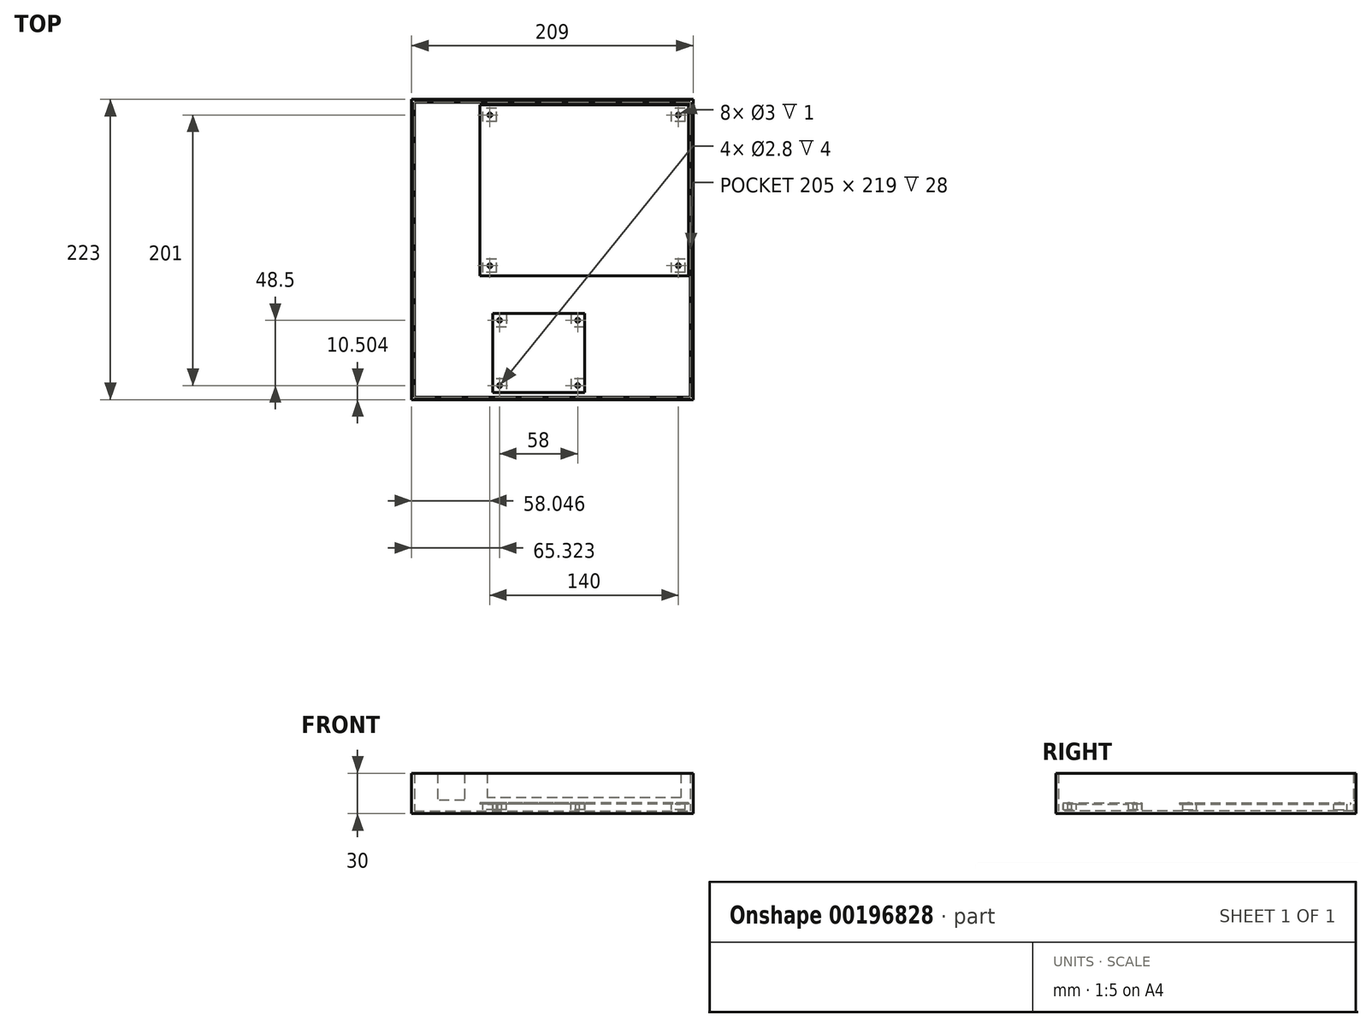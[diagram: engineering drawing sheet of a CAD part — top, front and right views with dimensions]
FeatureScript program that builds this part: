
annotation { "Feature Type Name" : "Feature", "Feature Type Description" : "" }
export const myFeature = defineFeature(function(context is Context, id is Id, definition is map)
    precondition{}
    {
        {
            var Q0;
            Q0=qCreatedBy(makeId("Top.planeOp"),FACE);
            var sketch = newSketch(context, id + "F0", { "sketchPlane" : qUnion([Q0])});
            skLineSegment(sketch, "E0.bottom", {"start": v(9.11, -36.76) * mm, "end": v(-58.89, -36.76) * mm});
            skLineSegment(sketch, "E0.top", {"start": v(9.11, 21.74) * mm, "end": v(-58.89, 21.74) * mm});
            skLineSegment(sketch, "E0.left", {"start": v(9.11, -36.76) * mm, "end": v(9.11, 21.74) * mm});
            skLineSegment(sketch, "E0.right", {"start": v(-58.89, -36.76) * mm, "end": v(-58.89, 21.74) * mm});
            skPoint(sketch, "E0.middle", {"position": v(-24.89, -7.5) * mm});
            skLineSegment(sketch, "E1.bottom", {"start": v(86.34, 49.74) * mm, "end": v(-68.66, 49.74) * mm});
            skLineSegment(sketch, "E1.top", {"start": v(86.34, 176.74) * mm, "end": v(-68.66, 176.74) * mm});
            skLineSegment(sketch, "E1.left", {"start": v(86.34, 49.74) * mm, "end": v(86.34, 176.74) * mm});
            skLineSegment(sketch, "E1.right", {"start": v(-68.66, 49.74) * mm, "end": v(-68.66, 176.74) * mm});
            skPoint(sketch, "E1.middle", {"position": v(8.84, 113.24) * mm});
            skLineSegment(sketch, "E2.bottom", {"start": v(-72.66, -35.95) * mm, "end": v(-114.66, -35.95) * mm, "construction": true});
            skLineSegment(sketch, "E2.top", {"start": v(-72.66, 141.05) * mm, "end": v(-114.66, 141.05) * mm, "construction": true});
            skLineSegment(sketch, "E2.left", {"start": v(-72.66, -35.95) * mm, "end": v(-72.66, 141.05) * mm, "construction": true});
            skLineSegment(sketch, "E2.right", {"start": v(-114.66, -35.95) * mm, "end": v(-114.66, 141.05) * mm, "construction": true});
            skPoint(sketch, "E2.middle", {"position": v(-93.66, 52.55) * mm});
            skLineSegment(sketch, "E3.bottom", {"start": v(-74.66, -33.95) * mm, "end": v(-112.66, -33.95) * mm, "construction": true});
            skLineSegment(sketch, "E3.top", {"start": v(-74.66, 139.05) * mm, "end": v(-112.66, 139.05) * mm, "construction": true});
            skLineSegment(sketch, "E3.left", {"start": v(-74.66, -33.95) * mm, "end": v(-74.66, 139.05) * mm, "construction": true});
            skLineSegment(sketch, "E3.right", {"start": v(-112.66, -33.95) * mm, "end": v(-112.66, 139.05) * mm, "construction": true});
            skSolve(sketch);
        }
        {
            var Q0;
            Q0 = qSketchRegion(id + "F0", true);
            extrude(context, id + "F1", {"entities" : qUnion([Q0]), "depth" : 1 * mm});
        }
        {
            var Q0;
            Q0=makeQuery(id+"F1.opExtrude","CAP_FACE",FACE,{"disambiguationData":[OSD([sQuery(id+"F0.wireOp",EDGE,"E0.bottom"),sQuery(id+"F0.wireOp",EDGE,"E0.top"),sQuery(id+"F0.wireOp",EDGE,"E0.left"),sQuery(id+"F0.wireOp",EDGE,"E0.right")])],"isStart":true});
            var sketch = newSketch(context, id + "F2", { "sketchPlane" : qUnion([Q0])});
            skLineSegment(sketch, "E4.bottom", {"start": v(-48.89, 26.76) * mm, "end": v(-58.89, 26.76) * mm});
            skLineSegment(sketch, "E4.top", {"start": v(-48.89, 36.76) * mm, "end": v(-58.89, 36.76) * mm});
            skLineSegment(sketch, "E4.left", {"start": v(-48.89, 26.76) * mm, "end": v(-48.89, 36.76) * mm});
            skLineSegment(sketch, "E4.right", {"start": v(-58.89, 26.76) * mm, "end": v(-58.89, 36.76) * mm});
            skPoint(sketch, "E4.middle", {"position": v(-53.89, 31.76) * mm});
            skLineSegment(sketch, "E5.bottom", {"start": v(9.11, 26.76) * mm, "end": v(-0.89, 26.76) * mm});
            skLineSegment(sketch, "E5.top", {"start": v(9.11, 36.76) * mm, "end": v(-0.89, 36.76) * mm});
            skLineSegment(sketch, "E5.left", {"start": v(9.11, 26.76) * mm, "end": v(9.11, 36.76) * mm});
            skLineSegment(sketch, "E5.right", {"start": v(-0.89, 26.76) * mm, "end": v(-0.89, 36.76) * mm});
            skPoint(sketch, "E5.middle", {"position": v(4.11, 31.76) * mm});
            skPoint(sketch, "E5.middle.positionSnap0", {"position": v(-48.89, 31.76) * mm});
            skPoint(sketch, "E5.centerSnap0", {"position": v(-48.89, 31.76) * mm});
            skLineSegment(sketch, "E6.bottom", {"start": v(-48.89, -21.74) * mm, "end": v(-58.89, -21.74) * mm});
            skLineSegment(sketch, "E6.top", {"start": v(-48.89, -11.74) * mm, "end": v(-58.89, -11.74) * mm});
            skLineSegment(sketch, "E6.left", {"start": v(-48.89, -21.74) * mm, "end": v(-48.89, -11.74) * mm});
            skLineSegment(sketch, "E6.right", {"start": v(-58.89, -21.74) * mm, "end": v(-58.89, -11.74) * mm});
            skPoint(sketch, "E6.middle", {"position": v(-53.89, -16.74) * mm});
            skLineSegment(sketch, "E7.bottom", {"start": v(9.11, -21.74) * mm, "end": v(-0.89, -21.74) * mm});
            skLineSegment(sketch, "E7.top", {"start": v(9.11, -11.74) * mm, "end": v(-0.89, -11.74) * mm});
            skLineSegment(sketch, "E7.left", {"start": v(9.11, -21.74) * mm, "end": v(9.11, -11.74) * mm});
            skLineSegment(sketch, "E7.right", {"start": v(-0.89, -21.74) * mm, "end": v(-0.89, -11.74) * mm});
            skPoint(sketch, "E7.middle", {"position": v(4.11, -16.74) * mm});
            skPoint(sketch, "E7.middle.positionSnap0", {"position": v(-48.89, -16.74) * mm});
            skPoint(sketch, "E7.centerSnap0", {"position": v(-48.89, -16.74) * mm});
            skCircle(sketch, "E8", {"center": v(-53.89, 31.76) * mm, "radius": 1.4 * mm});
            skCircle(sketch, "E9", {"center": v(4.11, 31.76) * mm, "radius": 1.4 * mm});
            skCircle(sketch, "E10", {"center": v(4.11, -16.74) * mm, "radius": 1.4 * mm});
            skCircle(sketch, "E11", {"center": v(-53.89, -16.74) * mm, "radius": 1.4 * mm});
            skLineSegment(sketch, "E12.bottom", {"start": v(-56.16, -164.24) * mm, "end": v(-66.16, -164.24) * mm});
            skLineSegment(sketch, "E12.top", {"start": v(-56.16, -174.24) * mm, "end": v(-66.16, -174.24) * mm});
            skLineSegment(sketch, "E12.left", {"start": v(-56.16, -164.24) * mm, "end": v(-56.16, -174.24) * mm});
            skLineSegment(sketch, "E12.right", {"start": v(-66.16, -164.24) * mm, "end": v(-66.16, -174.24) * mm});
            skPoint(sketch, "E12.middle", {"position": v(-61.16, -169.24) * mm});
            skLineSegment(sketch, "E13.bottom", {"start": v(83.84, -164.24) * mm, "end": v(73.84, -164.24) * mm});
            skLineSegment(sketch, "E13.top", {"start": v(83.84, -174.24) * mm, "end": v(73.84, -174.24) * mm});
            skLineSegment(sketch, "E13.left", {"start": v(83.84, -164.24) * mm, "end": v(83.84, -174.24) * mm});
            skLineSegment(sketch, "E13.right", {"start": v(73.84, -164.24) * mm, "end": v(73.84, -174.24) * mm});
            skPoint(sketch, "E13.middle", {"position": v(78.84, -169.24) * mm});
            skLineSegment(sketch, "E14.bottom", {"start": v(-56.16, -52.24) * mm, "end": v(-66.16, -52.24) * mm});
            skLineSegment(sketch, "E14.top", {"start": v(-56.16, -62.24) * mm, "end": v(-66.16, -62.24) * mm});
            skLineSegment(sketch, "E14.left", {"start": v(-56.16, -52.24) * mm, "end": v(-56.16, -62.24) * mm});
            skLineSegment(sketch, "E14.right", {"start": v(-66.16, -52.24) * mm, "end": v(-66.16, -62.24) * mm});
            skPoint(sketch, "E14.middle", {"position": v(-61.16, -57.24) * mm});
            skLineSegment(sketch, "E15.bottom", {"start": v(83.84, -52.24) * mm, "end": v(73.84, -52.24) * mm});
            skLineSegment(sketch, "E15.top", {"start": v(83.84, -62.24) * mm, "end": v(73.84, -62.24) * mm});
            skLineSegment(sketch, "E15.left", {"start": v(83.84, -52.24) * mm, "end": v(83.84, -62.24) * mm});
            skLineSegment(sketch, "E15.right", {"start": v(73.84, -52.24) * mm, "end": v(73.84, -62.24) * mm});
            skPoint(sketch, "E15.middle", {"position": v(78.84, -57.24) * mm});
            skPoint(sketch, "E15.middle.positionSnap0", {"position": v(78.84, -164.24) * mm});
            skPoint(sketch, "E15.middle.positionSnap1", {"position": v(-56.16, -57.24) * mm});
            skPoint(sketch, "E15.centerSnap0", {"position": v(78.84, -164.24) * mm});
            skPoint(sketch, "E15.centerSnap1", {"position": v(-56.16, -57.24) * mm});
            skSolve(sketch);
        }
        {
            var Q0;
            Q0 = qSketchRegion(id + "F2", true);
            extrude(context, id + "F3", {"entities" : qUnion([Q0]), "operationType" : NewBodyOperationType.ADD, "depth" : 4 * mm});
        }
        {
            var Q0;
            Q0=sQuery(id+"F2.wireOp",VERTEX,"E4.middle");
            var Q1;
            Q1=sQuery(id+"F2.wireOp",VERTEX,"E6.middle");
            var Q2;
            Q2=sQuery(id+"F2.wireOp",VERTEX,"E7.middle");
            var Q3;
            Q3=sQuery(id+"F2.wireOp",VERTEX,"E5.middle");
            var Q4;
            Q4=sQuery(id+"F2.wireOp",VERTEX,"E12.middle");
            var Q5;
            Q5=sQuery(id+"F2.wireOp",VERTEX,"E14.middle");
            var Q6;
            Q6=sQuery(id+"F2.wireOp",VERTEX,"E15.middle");
            var Q7;
            Q7=sQuery(id+"F2.wireOp",VERTEX,"E13.middle");
            var Q8;
            Q8=makeQuery(id+"F1.opExtrude","SWEPT_BODY",BODY,{"disambiguationData":[OSD([sQuery(id+"F0.wireOp",EDGE,"E0.bottom"),sQuery(id+"F0.wireOp",EDGE,"E0.top"),sQuery(id+"F0.wireOp",EDGE,"E0.left"),sQuery(id+"F0.wireOp",EDGE,"E0.right")])]});
            var Q9;
            Q9=makeQuery(id+"F1.opExtrude","SWEPT_BODY",BODY,{"disambiguationData":[OSD([sQuery(id+"F0.wireOp",EDGE,"E1.bottom"),sQuery(id+"F0.wireOp",EDGE,"E1.top"),sQuery(id+"F0.wireOp",EDGE,"E1.left"),sQuery(id+"F0.wireOp",EDGE,"E1.right")])]});
            hole(context, id + "F4", {"style" : HoleStyle.SIMPLE, "endStyle" : HoleEndStyle.BLIND, "holeDiameter" : 3 * mm, "holeDepth" : 3 * mm, "locations" : qUnion([Q0, Q1, Q2, Q3, Q4, Q5, Q6, Q7]), "scope" : qUnion([Q8, Q9])});
        }
        {
            var Q0;
            Q0=qCreatedBy(makeId("Top.planeOp"),FACE);
            cPlane(context, id + "F5", {"entities" : qUnion([Q0]), "cplaneType" : CPlaneType.OFFSET, "offset" : 7 * mm, "oppositeDirection" : true, "width" : 150 * mm, "height" : 150 * mm});
        }
        {
            var Q0;
            Q0=qCreatedBy(id+"F5.planeOp",FACE);
            var sketch = newSketch(context, id + "F6", { "sketchPlane" : qUnion([Q0])});
            skLineSegment(sketch, "E16.bottom", {"start": v(-119.2, 180.74) * mm, "end": v(89.8, 180.74) * mm});
            skLineSegment(sketch, "E16.top", {"start": v(-119.2, -42.26) * mm, "end": v(89.8, -42.26) * mm});
            skLineSegment(sketch, "E16.left", {"start": v(-119.2, 180.74) * mm, "end": v(-119.2, -42.26) * mm});
            skLineSegment(sketch, "E16.right", {"start": v(89.8, 180.74) * mm, "end": v(89.8, -42.26) * mm});
            skSolve(sketch);
        }
        {
            var Q0;
            Q0 = qSketchRegion(id + "F6", true);
            extrude(context, id + "F7", {"entities" : qUnion([Q0]), "depth" : 30 * mm});
        }
        {
            var Q0;
            Q0=makeQuery(id+"F7.opExtrude","CAP_FACE",FACE,{"disambiguationData":[OSD([sQuery(id+"F6.wireOp",EDGE,"E16.bottom"),sQuery(id+"F6.wireOp",EDGE,"E16.top"),sQuery(id+"F6.wireOp",EDGE,"E16.left"),sQuery(id+"F6.wireOp",EDGE,"E16.right")])],"isStart":false});
            shell(context, id + "F8", {"entities" : qUnion([Q0]), "thickness" : 2 * mm});
        }
        {
            var Q0;
            Q0=makeQuery(id+"F7.opExtrude","SWEPT_FACE",FACE,{"disambiguationData":[OSD([sQuery(id+"F6.wireOp",EDGE,"E16.bottom")])]});
            var sketch = newSketch(context, id + "F9", { "sketchPlane" : qUnion([Q0])});
            skLineSegment(sketch, "E17.bottom", {"start": v(-80.84, 23) * mm, "end": v(63.16, 23) * mm});
            skLineSegment(sketch, "E17.top", {"start": v(-80.84, 5) * mm, "end": v(63.16, 5) * mm});
            skLineSegment(sketch, "E17.left", {"start": v(-80.84, 23) * mm, "end": v(-80.84, 5) * mm});
            skLineSegment(sketch, "E17.right", {"start": v(63.16, 23) * mm, "end": v(63.16, 5) * mm});
            skLineSegment(sketch, "E18.bottom", {"start": v(79.84, 23) * mm, "end": v(99.84, 23) * mm});
            skLineSegment(sketch, "E18.top", {"start": v(79.84, 2.88) * mm, "end": v(99.84, 2.88) * mm});
            skLineSegment(sketch, "E18.left", {"start": v(79.84, 23) * mm, "end": v(79.84, 2.88) * mm});
            skLineSegment(sketch, "E18.right", {"start": v(99.84, 23) * mm, "end": v(99.84, 2.88) * mm});
            skSolve(sketch);
        }
        {
            var Q0;
            Q0 = qSketchRegion(id + "F9", true);
            extrude(context, id + "F10", {"entities" : qUnion([Q0]), "operationType" : NewBodyOperationType.REMOVE, "oppositeDirection" : true, "depth" : 2 * mm});
        }
    });
